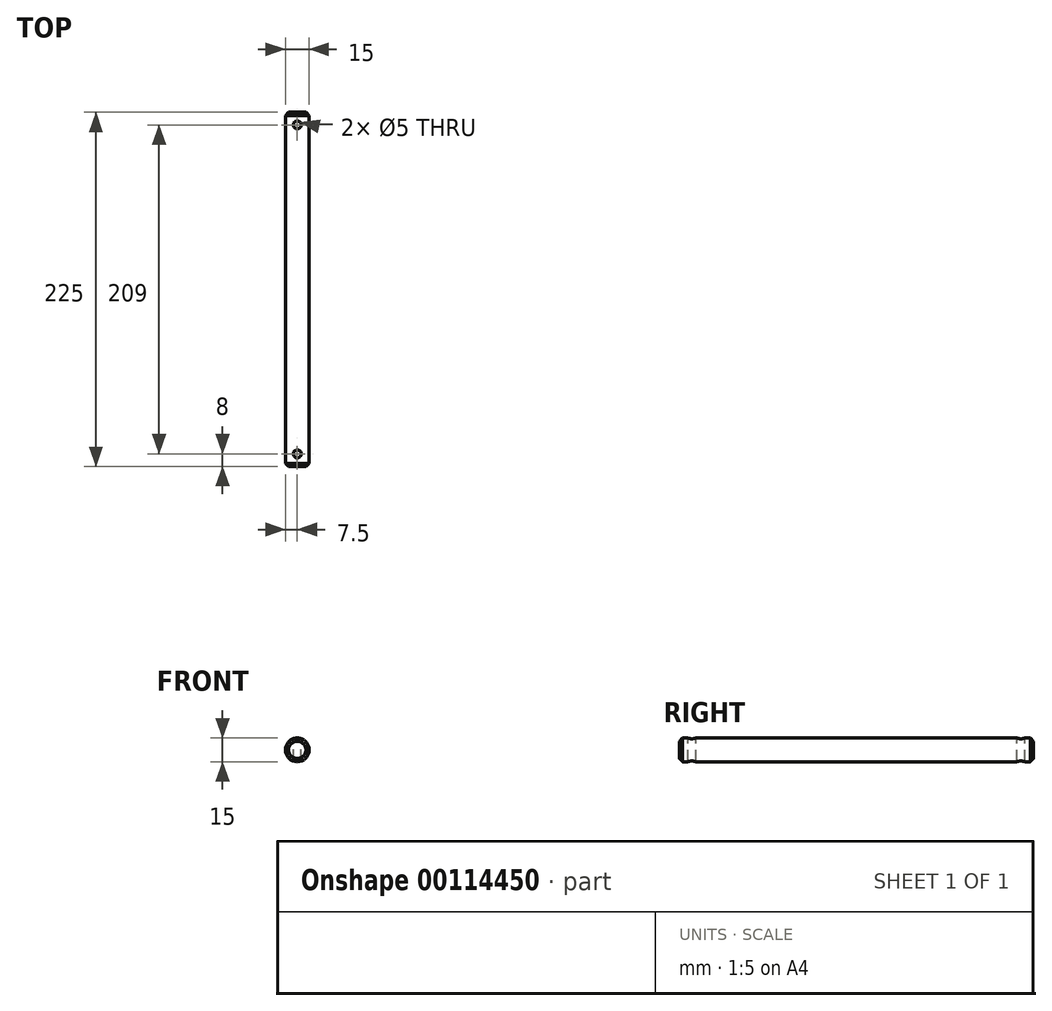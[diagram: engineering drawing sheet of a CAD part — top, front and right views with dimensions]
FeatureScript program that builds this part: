
annotation { "Feature Type Name" : "Feature", "Feature Type Description" : "" }
export const myFeature = defineFeature(function(context is Context, id is Id, definition is map)
    precondition{}
    {
        {
            var Q0;
            Q0=qCreatedBy(makeId("Front.planeOp"),FACE);
            var sketch = newSketch(context, id + "F0", { "sketchPlane" : qUnion([Q0])});
            skCircle(sketch, "E0", {"center": v(0, 0) * mm, "radius": 7.5 * mm});
            skSolve(sketch);
        }
        {
            var Q0;
            Q0 = qSketchRegion(id + "F0", true);
            extrude(context, id + "F1", {"entities" : qUnion([Q0]), "depth" : 225 * mm});
        }
        {
            var Q0;
            Q0=qCreatedBy(makeId("Top.planeOp"),FACE);
            cPlane(context, id + "F2", {"entities" : qUnion([Q0]), "cplaneType" : CPlaneType.OFFSET, "offset" : 7.5 * mm, "width" : 150 * mm, "height" : 150 * mm});
        }
        {
            var Q0;
            Q0=qCreatedBy(id+"F2.planeOp",FACE);
            var sketch = newSketch(context, id + "F3", { "sketchPlane" : qUnion([Q0])});
            skCircle(sketch, "E1", {"center": v(0, -8) * mm, "radius": 2.5 * mm});
            skCircle(sketch, "E2", {"center": v(0, -217) * mm, "radius": 2.5 * mm});
            skSolve(sketch);
        }
        {
            var Q0;
            Q0=makeQuery(id+"F3.imprint","IMPRINT",FACE,{"disambiguationData":[TD([[makeQuery(id+"F3.imprint","IMPRINT",EDGE,{"derivedFrom":sQuery(id+"F3.wireOp",EDGE,"E1")}),1.0]])]});
            var Q1;
            Q1=makeQuery(id+"F3.imprint","IMPRINT",FACE,{"disambiguationData":[TD([[makeQuery(id+"F3.imprint","IMPRINT",EDGE,{"derivedFrom":sQuery(id+"F3.wireOp",EDGE,"E2")}),1.0]])]});
            extrude(context, id + "F4", {"entities" : qUnion([Q0, Q1]), "operationType" : NewBodyOperationType.REMOVE, "endBound" : BoundingType.THROUGH_ALL, "oppositeDirection" : true, "depth" : 25 * mm});
        }
        {
            var Q0;
            Q0=makeQuery(id+"F1.opExtrude","CAP_EDGE",EDGE,{"disambiguationData":[OSD([sQuery(id+"F0.wireOp",EDGE,"E0")])],"isStart":false});
            chamfer(context, id + "F5", {"entities" : qUnion([Q0]), "width" : 2 * mm, "tangentPropagation" : true});
        }
        {
            var Q0;
            Q0=makeQuery(id+"F1.opExtrude","CAP_EDGE",EDGE,{"disambiguationData":[OSD([sQuery(id+"F0.wireOp",EDGE,"E0")])],"isStart":true});
            chamfer(context, id + "F6", {"entities" : qUnion([Q0]), "width" : 2 * mm, "tangentPropagation" : true});
        }
    });
